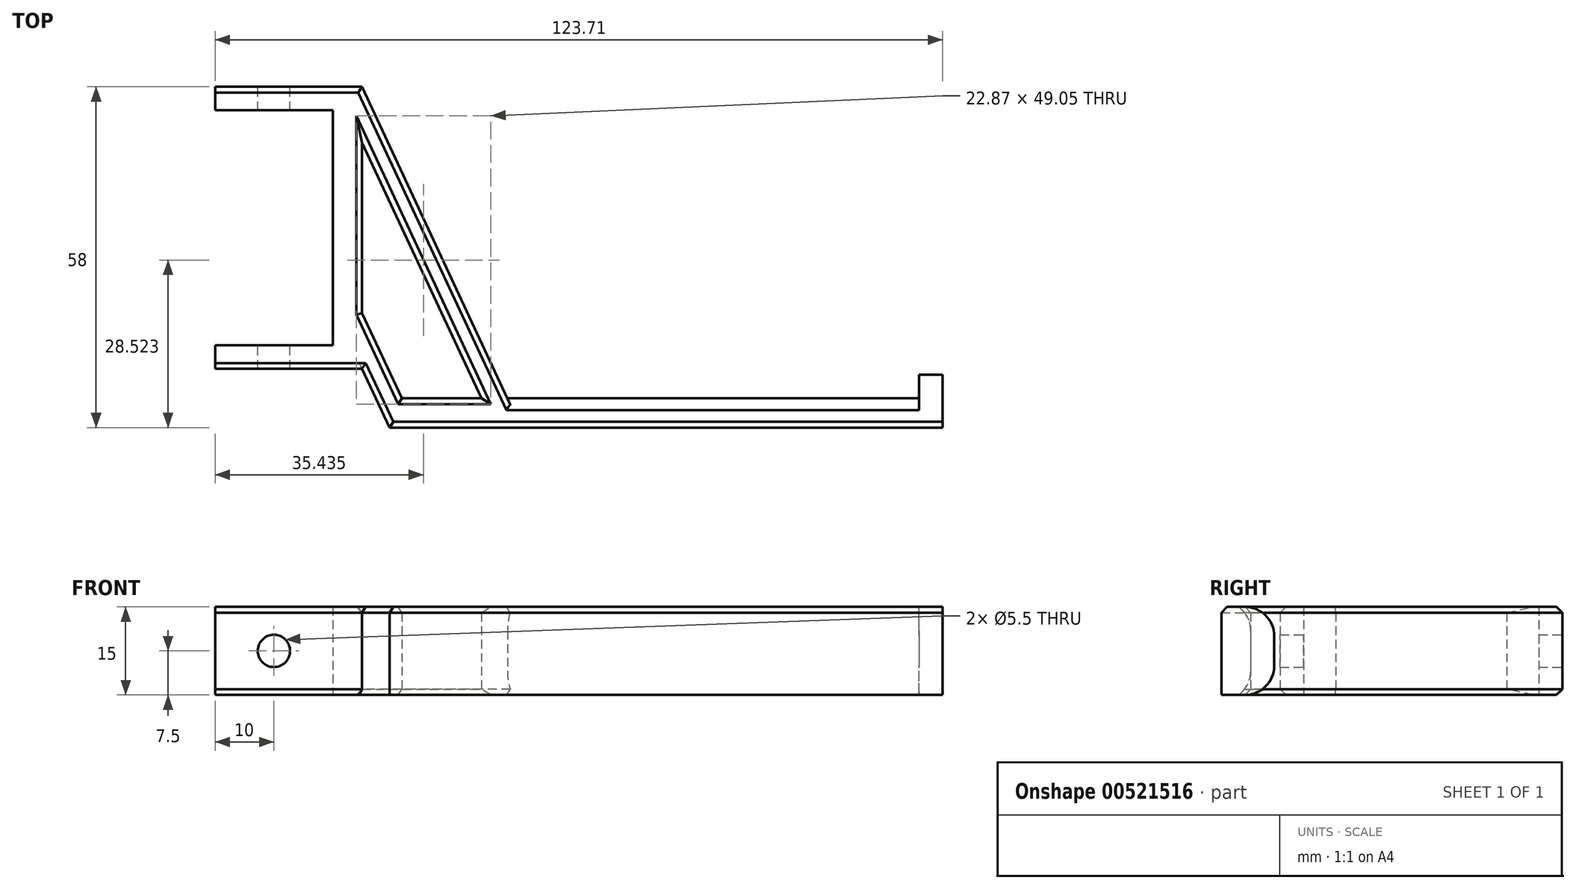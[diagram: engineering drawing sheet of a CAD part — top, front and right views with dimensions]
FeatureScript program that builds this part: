
annotation { "Feature Type Name" : "Feature", "Feature Type Description" : "" }
export const myFeature = defineFeature(function(context is Context, id is Id, definition is map)
    precondition{}
    {
        {
            var Q0;
            Q0=qCreatedBy(makeId("Top.planeOp"),FACE);
            var sketch = newSketch(context, id + "F0", { "sketchPlane" : qUnion([Q0])});
            skLineSegment(sketch, "E0", {"start": v(0, 0) * mm, "end": v(20, 0) * mm});
            skLineSegment(sketch, "E1", {"start": v(20, 0) * mm, "end": v(20, -40) * mm});
            skLineSegment(sketch, "E2", {"start": v(20, -40) * mm, "end": v(0, -40) * mm});
            skLineSegment(sketch, "E3", {"start": v(0, -40) * mm, "end": v(0, -44) * mm});
            skLineSegment(sketch, "E4", {"start": v(123.71, -54) * mm, "end": v(123.71, -45) * mm});
            skLineSegment(sketch, "E5", {"start": v(123.71, -45) * mm, "end": v(119.71, -45) * mm});
            skLineSegment(sketch, "E6", {"start": v(119.71, -45) * mm, "end": v(119.71, -49) * mm});
            skLineSegment(sketch, "E7", {"start": v(119.71, -49) * mm, "end": v(49.71, -49) * mm});
            skLineSegment(sketch, "E8", {"start": v(49.71, -49) * mm, "end": v(25, 4) * mm});
            skLineSegment(sketch, "E9", {"start": v(25, 4) * mm, "end": v(0, 4) * mm});
            skLineSegment(sketch, "E10", {"start": v(0, 4) * mm, "end": v(0, 0) * mm});
            skLineSegment(sketch, "E11", {"start": v(123.71, -54) * mm, "end": v(29.66, -54) * mm});
            skLineSegment(sketch, "E12", {"start": v(29.66, -54) * mm, "end": v(25, -44) * mm});
            skLineSegment(sketch, "E13", {"start": v(25, -44) * mm, "end": v(0, -44) * mm});
            skLineSegment(sketch, "E14", {"start": v(25, -5.46) * mm, "end": v(45.3, -49) * mm});
            skLineSegment(sketch, "E15", {"start": v(45.3, -49) * mm, "end": v(31.75, -49) * mm});
            skLineSegment(sketch, "E16", {"start": v(31.75, -49) * mm, "end": v(25, -34.54) * mm});
            skLineSegment(sketch, "E17", {"start": v(25, -34.54) * mm, "end": v(25, -5.46) * mm});
            skSolve(sketch);
        }
        {
            var Q0;
            Q0 = qSketchRegion(id + "F0", true);
            extrude(context, id + "F1", {"entities" : qUnion([Q0]), "depth" : 15 * mm, "offsetDistance" : 25 * mm});
        }
        {
            var Q0;
            Q0=makeQuery(id+"F1.opExtrude","CAP_EDGE",EDGE,{"disambiguationData":[OSD([sQuery(id+"F0.wireOp",EDGE,"E15")])],"isStart":false});
            var Q1;
            Q1=makeQuery(id+"F1.opExtrude","CAP_EDGE",EDGE,{"disambiguationData":[OSD([sQuery(id+"F0.wireOp",EDGE,"E16")])],"isStart":false});
            var Q2;
            Q2=makeQuery(id+"F1.opExtrude","CAP_EDGE",EDGE,{"disambiguationData":[OSD([sQuery(id+"F0.wireOp",EDGE,"E17")])],"isStart":false});
            var Q3;
            Q3=makeQuery(id+"F1.opExtrude","CAP_EDGE",EDGE,{"disambiguationData":[OSD([sQuery(id+"F0.wireOp",EDGE,"E14")])],"isStart":false});
            var Q4;
            Q4=makeQuery(id+"F1.opExtrude","CAP_EDGE",EDGE,{"disambiguationData":[OSD([sQuery(id+"F0.wireOp",EDGE,"E8")])],"isStart":false});
            var Q5;
            Q5=makeQuery(id+"F1.opExtrude","CAP_EDGE",EDGE,{"disambiguationData":[OSD([sQuery(id+"F0.wireOp",EDGE,"E14")])],"isStart":true});
            var Q6;
            Q6=makeQuery(id+"F1.opExtrude","CAP_EDGE",EDGE,{"disambiguationData":[OSD([sQuery(id+"F0.wireOp",EDGE,"E17")])],"isStart":true});
            var Q7;
            Q7=makeQuery(id+"F1.opExtrude","CAP_EDGE",EDGE,{"disambiguationData":[OSD([sQuery(id+"F0.wireOp",EDGE,"E16")])],"isStart":true});
            var Q8;
            Q8=makeQuery(id+"F1.opExtrude","CAP_EDGE",EDGE,{"disambiguationData":[OSD([sQuery(id+"F0.wireOp",EDGE,"E15")])],"isStart":true});
            var Q9;
            Q9=makeQuery(id+"F1.opExtrude","CAP_EDGE",EDGE,{"disambiguationData":[OSD([sQuery(id+"F0.wireOp",EDGE,"E12")])],"isStart":false});
            var Q10;
            Q10=makeQuery(id+"F1.opExtrude","CAP_EDGE",EDGE,{"disambiguationData":[OSD([sQuery(id+"F0.wireOp",EDGE,"E11")])],"isStart":false});
            var Q11;
            Q11=makeQuery(id+"F1.opExtrude","CAP_EDGE",EDGE,{"disambiguationData":[OSD([sQuery(id+"F0.wireOp",EDGE,"E13")])],"isStart":false});
            var Q12;
            Q12=makeQuery(id+"F1.opExtrude","CAP_EDGE",EDGE,{"disambiguationData":[OSD([sQuery(id+"F0.wireOp",EDGE,"E9")])],"isStart":false});
            var Q13;
            Q13=makeQuery(id+"F1.opExtrude","CAP_EDGE",EDGE,{"disambiguationData":[OSD([sQuery(id+"F0.wireOp",EDGE,"E13")])],"isStart":true});
            var Q14;
            Q14=makeQuery(id+"F1.opExtrude","CAP_EDGE",EDGE,{"disambiguationData":[OSD([sQuery(id+"F0.wireOp",EDGE,"E9")])],"isStart":true});
            var Q15;
            Q15=makeQuery(id+"F1.opExtrude","CAP_EDGE",EDGE,{"disambiguationData":[OSD([sQuery(id+"F0.wireOp",EDGE,"E8")])],"isStart":true});
            chamfer(context, id + "F2", {"entities" : qUnion([Q0, Q1, Q2, Q3, Q4, Q5, Q6, Q7, Q8, Q9, Q10, Q11, Q12, Q13, Q14, Q15]), "width" : 1 * mm, "tangentPropagation" : true});
        }
        {
            var Q0;
            Q0=makeQuery(id+"F1.opExtrude","CAP_EDGE",EDGE,{"disambiguationData":[OSD([sQuery(id+"F0.wireOp",EDGE,"E7")])],"isStart":false});
            var Q1;
            Q1=makeQuery(id+"F1.opExtrude","CAP_EDGE",EDGE,{"disambiguationData":[OSD([sQuery(id+"F0.wireOp",EDGE,"E7")])],"isStart":true});
            chamfer(context, id + "F3", {"entities" : qUnion([Q0, Q1]), "width" : 2 * mm, "tangentPropagation" : true});
        }
        {
            var Q0;
            {var subQ0=sQuery(id+"F0.wireOp",EDGE,"E7");Q0=makeQuery(id+"F3.opChamfer","BLEND_EDGE",EDGE,{"blendedFrom":[makeQuery(id+"F1.opExtrude","CAP_EDGE",EDGE,{"disambiguationData":[OSD([subQ0])],"isStart":true}),makeQuery(id+"F1.opExtrude","SWEPT_FACE",FACE,{"disambiguationData":[OSD([subQ0])]})],"blendedInto":[makeQuery(id+"F1.opExtrude","SWEPT_FACE",FACE,{"disambiguationData":[OSD([subQ0])]})]});}
            var Q1;
            {var subQ0=sQuery(id+"F0.wireOp",EDGE,"E7");Q1=makeQuery(id+"F3.opChamfer","BLEND_EDGE",EDGE,{"blendedFrom":[makeQuery(id+"F1.opExtrude","CAP_EDGE",EDGE,{"disambiguationData":[OSD([subQ0])],"isStart":false}),makeQuery(id+"F1.opExtrude","SWEPT_FACE",FACE,{"disambiguationData":[OSD([subQ0])]})],"blendedInto":[makeQuery(id+"F1.opExtrude","SWEPT_FACE",FACE,{"disambiguationData":[OSD([subQ0])]})]});}
            var Q2;
            Q2=makeQuery(id+"F1.opExtrude","CAP_EDGE",EDGE,{"disambiguationData":[OSD([sQuery(id+"F0.wireOp",EDGE,"E5")])],"isStart":true});
            var Q3;
            Q3=makeQuery(id+"F1.opExtrude","CAP_EDGE",EDGE,{"disambiguationData":[OSD([sQuery(id+"F0.wireOp",EDGE,"E5")])],"isStart":false});
            fillet(context, id + "F4", {"entities" : qUnion([Q0, Q1, Q2, Q3]), "radius" : 5 * mm, "tangentPropagation" : true, "allowEdgeOverflow" : false});
        }
        {
            var Q0;
            Q0=makeQuery(id+"F1.opExtrude","SWEPT_FACE",FACE,{"disambiguationData":[OSD([sQuery(id+"F0.wireOp",EDGE,"E9")])]});
            var sketch = newSketch(context, id + "F5", { "sketchPlane" : qUnion([Q0])});
            skLineSegment(sketch, "E18.0.0", {"start": v(-20, 14) * mm, "end": v(-20, 1) * mm, "construction": true});
            skLineSegment(sketch, "E18.0.1", {"start": v(-20, 1) * mm, "end": v(0, 1) * mm, "construction": true});
            skLineSegment(sketch, "E18.0.2", {"start": v(0, 1) * mm, "end": v(0, 14) * mm, "construction": true});
            skLineSegment(sketch, "E18.0.3", {"start": v(0, 14) * mm, "end": v(-20, 14) * mm, "construction": true});
            skCircle(sketch, "E19", {"center": v(-10, 7.5) * mm, "radius": 2.75 * mm});
            skPoint(sketch, "E19.centerSnap0", {"position": v(-20, 7.5) * mm});
            skSolve(sketch);
        }
        {
            var Q0;
            Q0 = qSketchRegion(id + "F5", true);
            extrude(context, id + "F6", {"entities" : qUnion([Q0]), "operationType" : NewBodyOperationType.REMOVE, "endBound" : BoundingType.THROUGH_ALL, "oppositeDirection" : true, "depth" : 25 * mm, "offsetDistance" : 25 * mm});
        }
    });
